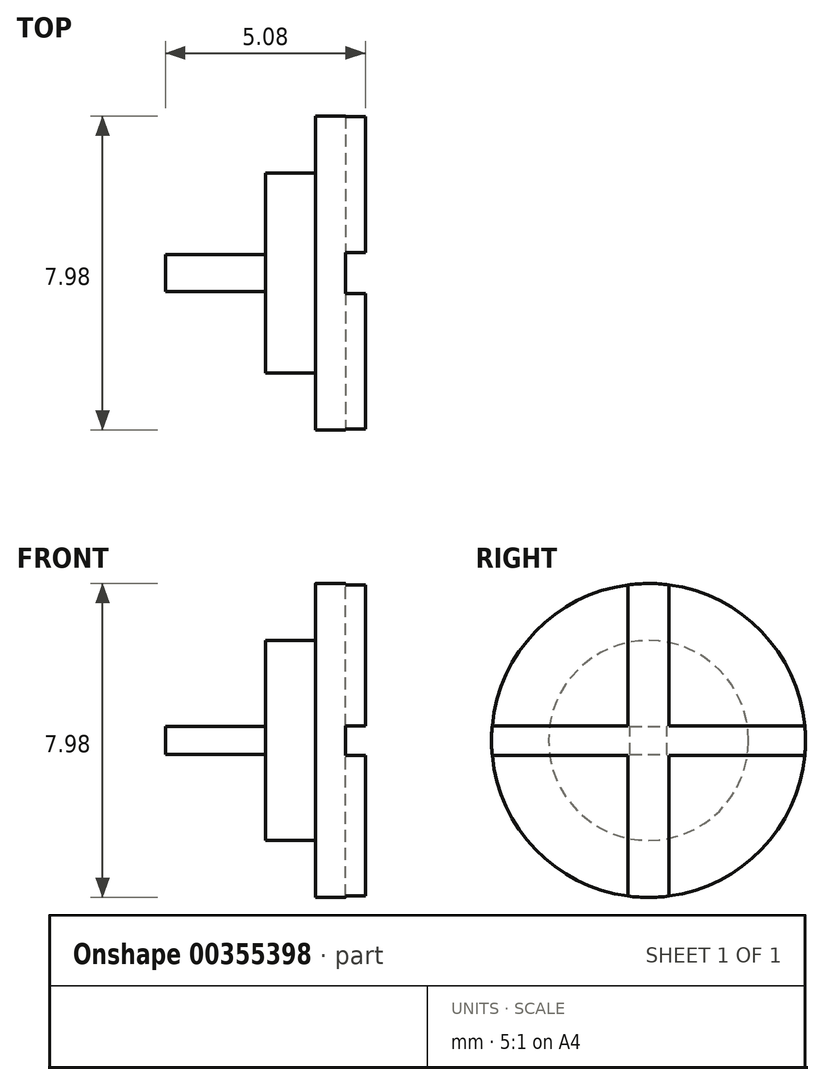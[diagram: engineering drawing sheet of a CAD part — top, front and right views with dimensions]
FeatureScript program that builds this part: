
annotation { "Feature Type Name" : "Feature", "Feature Type Description" : "" }
export const myFeature = defineFeature(function(context is Context, id is Id, definition is map)
    precondition{}
    {
        {
            var Q0;
            Q0=qCreatedBy(makeId("Right.planeOp"),FACE);
            var sketch = newSketch(context, id + "F0", { "sketchPlane" : qUnion([Q0])});
            skCircle(sketch, "E0", {"center": v(-2.84, 0.8) * mm, "radius": 2.54 * mm});
            skSolve(sketch);
        }
        {
            var Q0;
            Q0 = qSketchRegion(id + "F0", true);
            extrude(context, id + "F1", {"entities" : qUnion([Q0]), "depth" : 1.27 * mm});
        }
        {
            var Q0;
            Q0=makeQuery(id+"F1.opExtrude","CAP_FACE",FACE,{"disambiguationData":[OSD([sQuery(id+"F0.wireOp",EDGE,"E0")])],"isStart":false});
            var sketch = newSketch(context, id + "F2", { "sketchPlane" : qUnion([Q0])});
            skCircle(sketch, "E1", {"center": v(-2.84, 0.8) * mm, "radius": 3.99 * mm});
            skSolve(sketch);
        }
        {
            var Q0;
            Q0 = qSketchRegion(id + "F2", true);
            extrude(context, id + "F3", {"entities" : qUnion([Q0]), "operationType" : NewBodyOperationType.ADD, "depth" : 1.27 * mm});
        }
        {
            var Q0;
            Q0=makeQuery(id+"F1.opExtrude","CAP_FACE",FACE,{"disambiguationData":[OSD([sQuery(id+"F0.wireOp",EDGE,"E0")])],"isStart":true});
            var sketch = newSketch(context, id + "F4", { "sketchPlane" : qUnion([Q0])});
            skLineSegment(sketch, "E2.bottom", {"start": v(3.3, 0.44) * mm, "end": v(2.37, 0.44) * mm});
            skLineSegment(sketch, "E2.top", {"start": v(3.3, 1.16) * mm, "end": v(2.37, 1.16) * mm});
            skLineSegment(sketch, "E2.left", {"start": v(3.3, 0.44) * mm, "end": v(3.3, 1.16) * mm});
            skLineSegment(sketch, "E2.right", {"start": v(2.37, 0.44) * mm, "end": v(2.37, 1.16) * mm});
            skPoint(sketch, "E2.middle", {"position": v(2.84, 0.8) * mm});
            skSolve(sketch);
        }
        {
            var Q0;
            Q0 = qSketchRegion(id + "F4", true);
            extrude(context, id + "F5", {"entities" : qUnion([Q0]), "operationType" : NewBodyOperationType.ADD, "depth" : 2.54 * mm});
        }
        {
            var Q0;
            Q0=makeQuery(id+"F3.opExtrude","CAP_FACE",FACE,{"disambiguationData":[OSD([sQuery(id+"F2.wireOp",EDGE,"E1")])],"isStart":false});
            var sketch = newSketch(context, id + "F6", { "sketchPlane" : qUnion([Q0])});
            skLineSegment(sketch, "E3.bottom", {"start": v(-2.32, -3.5) * mm, "end": v(-3.36, -3.5) * mm});
            skLineSegment(sketch, "E3.top", {"start": v(-2.32, 5.1) * mm, "end": v(-3.36, 5.1) * mm});
            skLineSegment(sketch, "E3.left", {"start": v(-2.32, -3.5) * mm, "end": v(-2.32, 5.1) * mm});
            skLineSegment(sketch, "E3.right", {"start": v(-3.36, -3.5) * mm, "end": v(-3.36, 5.1) * mm});
            skPoint(sketch, "E3.middle", {"position": v(-2.84, 0.8) * mm});
            skLineSegment(sketch, "E4.bottom", {"start": v(1.6, 1.18) * mm, "end": v(-7.27, 1.18) * mm});
            skLineSegment(sketch, "E4.top", {"start": v(1.6, 0.43) * mm, "end": v(-7.27, 0.43) * mm});
            skLineSegment(sketch, "E4.left", {"start": v(1.6, 1.18) * mm, "end": v(1.6, 0.43) * mm});
            skLineSegment(sketch, "E4.right", {"start": v(-7.27, 1.18) * mm, "end": v(-7.27, 0.43) * mm});
            skSolve(sketch);
        }
        {
            var Q0;
            {var subQ0=sQuery(id+"F6.wireOp",EDGE,"E4.bottom");var subQ1=sQuery(id+"F6.wireOp",EDGE,"E3.left");var subQ2=makeQuery(id+"F6.imprint","INTERSECT",VERTEX,{"derivedFrom":[subQ1,subQ0]});Q0=makeQuery(id+"F6.imprint","IMPRINT",FACE,{"disambiguationData":[TD([[makeQuery(id+"F6.imprint","IMPRINT",EDGE,{"disambiguationData":[TD([[subQ2,-1.0]])],"derivedFrom":subQ1}),1.0]])]});}
            var Q1;
            {var subQ0=sQuery(id+"F6.wireOp",EDGE,"E4.top");var subQ1=sQuery(id+"F6.wireOp",EDGE,"E3.left");var subQ2=makeQuery(id+"F6.imprint","INTERSECT",VERTEX,{"derivedFrom":[subQ1,subQ0]});Q1=makeQuery(id+"F6.imprint","IMPRINT",FACE,{"disambiguationData":[TD([[makeQuery(id+"F6.imprint","IMPRINT",EDGE,{"disambiguationData":[TD([[subQ2,-1.0]])],"derivedFrom":subQ1}),-1.0]])]});}
            var Q2;
            {var subQ0=sQuery(id+"F6.wireOp",EDGE,"E4.top");var subQ1=sQuery(id+"F6.wireOp",EDGE,"E3.left");var subQ2=makeQuery(id+"F6.imprint","INTERSECT",VERTEX,{"derivedFrom":[subQ1,subQ0]});Q2=makeQuery(id+"F6.imprint","IMPRINT",FACE,{"disambiguationData":[TD([[makeQuery(id+"F6.imprint","IMPRINT",EDGE,{"disambiguationData":[TD([[subQ2,1.0]])],"derivedFrom":subQ1}),1.0]])]});}
            var Q3;
            {var subQ0=sQuery(id+"F6.wireOp",EDGE,"E4.top");var subQ1=sQuery(id+"F6.wireOp",EDGE,"E3.right");var subQ2=makeQuery(id+"F6.imprint","INTERSECT",VERTEX,{"derivedFrom":[subQ1,subQ0]});Q3=makeQuery(id+"F6.imprint","IMPRINT",FACE,{"disambiguationData":[TD([[makeQuery(id+"F6.imprint","IMPRINT",EDGE,{"disambiguationData":[TD([[subQ2,-1.0]])],"derivedFrom":subQ1}),1.0]])]});}
            var Q4;
            {var subQ0=sQuery(id+"F6.wireOp",EDGE,"E4.top");var subQ1=sQuery(id+"F6.wireOp",EDGE,"E3.left");var subQ2=makeQuery(id+"F6.imprint","INTERSECT",VERTEX,{"derivedFrom":[subQ1,subQ0]});Q4=makeQuery(id+"F6.imprint","IMPRINT",FACE,{"disambiguationData":[TD([[makeQuery(id+"F6.imprint","IMPRINT",EDGE,{"disambiguationData":[TD([[subQ2,-1.0]])],"derivedFrom":subQ1}),1.0]])]});}
            extrude(context, id + "F7", {"entities" : qUnion([Q0, Q1, Q2, Q3, Q4]), "operationType" : NewBodyOperationType.REMOVE, "oppositeDirection" : true, "depth" : 0.5 * mm});
        }
    });
